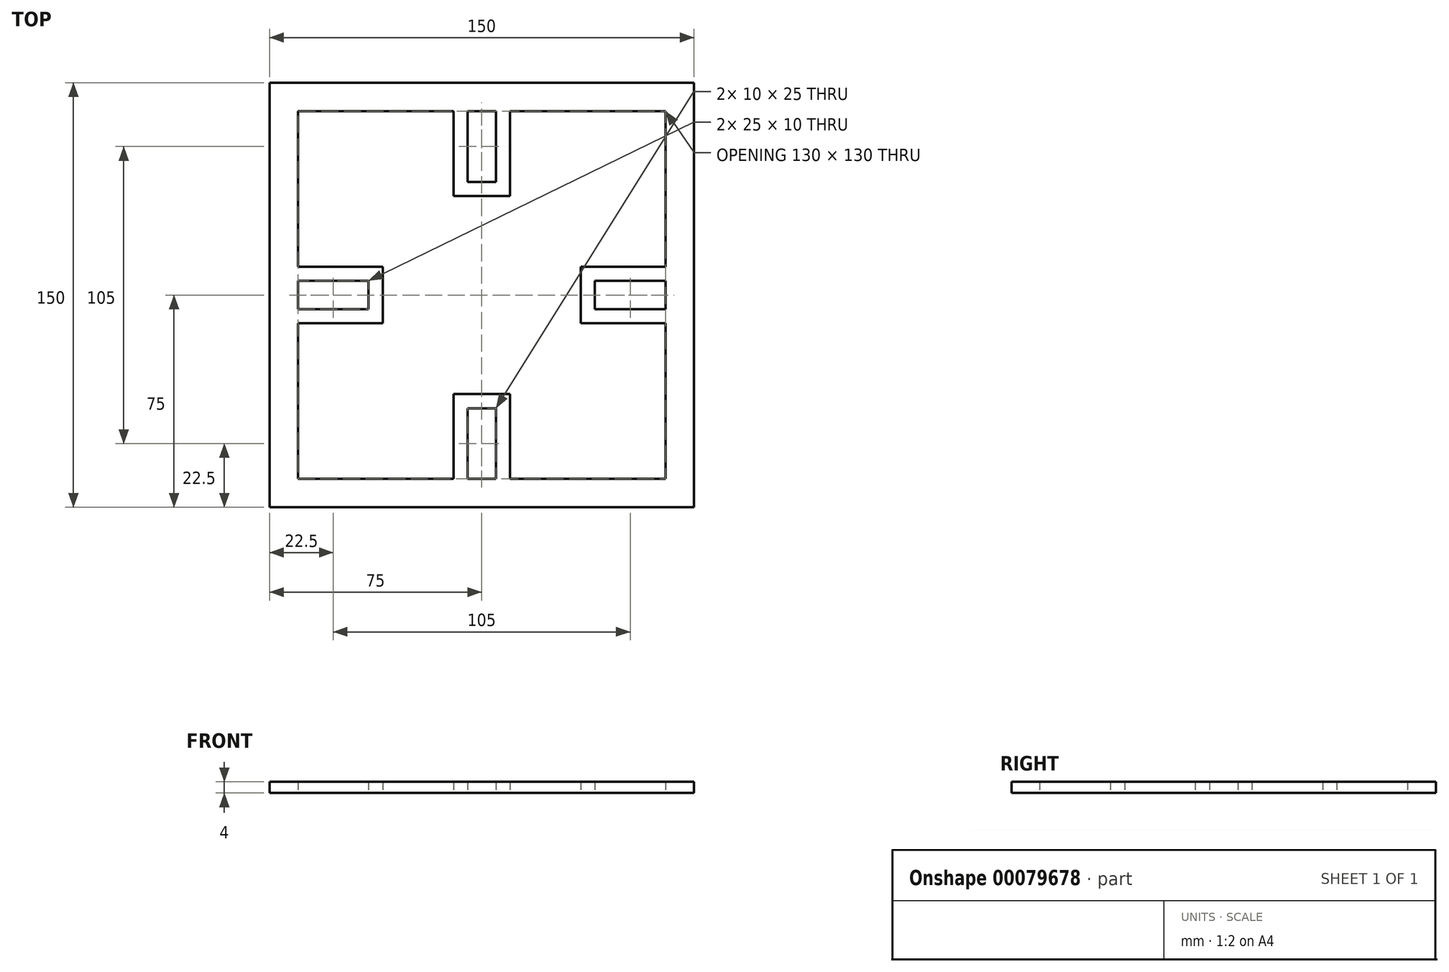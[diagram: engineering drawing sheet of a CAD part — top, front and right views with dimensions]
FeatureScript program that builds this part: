
annotation { "Feature Type Name" : "Feature", "Feature Type Description" : "" }
export const myFeature = defineFeature(function(context is Context, id is Id, definition is map)
    precondition{}
    {
        {
            var Q0;
            Q0=qCreatedBy(makeId("Top.planeOp"),FACE);
            var sketch = newSketch(context, id + "F0", { "sketchPlane" : qUnion([Q0])});
            skLineSegment(sketch, "E0.bottom", {"start": v(-75, 75) * mm, "end": v(75, 75) * mm});
            skLineSegment(sketch, "E0.top", {"start": v(-75, -75) * mm, "end": v(75, -75) * mm});
            skLineSegment(sketch, "E0.left", {"start": v(-75, 75) * mm, "end": v(-75, -75) * mm});
            skLineSegment(sketch, "E0.right", {"start": v(75, 75) * mm, "end": v(75, -75) * mm});
            skPoint(sketch, "E1", {"position": v(-75, 0) * mm});
            skPoint(sketch, "E2", {"position": v(0, 75) * mm});
            skLineSegment(sketch, "E3.bottom", {"start": v(-65, 65) * mm, "end": v(65, 65) * mm});
            skLineSegment(sketch, "E3.top", {"start": v(-65, -65) * mm, "end": v(65, -65) * mm});
            skLineSegment(sketch, "E3.left", {"start": v(-65, 65) * mm, "end": v(-65, -65) * mm});
            skLineSegment(sketch, "E3.right", {"start": v(65, 65) * mm, "end": v(65, -65) * mm});
            skSolve(sketch);
        }
        {
            var Q0;
            Q0=makeQuery(id+"F0.imprint","IMPRINT",FACE,{"disambiguationData":[TD([[makeQuery(id+"F0.imprint","IMPRINT",EDGE,{"derivedFrom":sQuery(id+"F0.wireOp",EDGE,"E0.bottom")}),-1.0]])]});
            extrude(context, id + "F1", {"entities" : qUnion([Q0]), "depth" : 4 * mm});
        }
        {
            var Q0;
            Q0=qCreatedBy(makeId("Top.planeOp"),FACE);
            var sketch = newSketch(context, id + "F2", { "sketchPlane" : qUnion([Q0])});
            skLineSegment(sketch, "E4.bottom", {"start": v(-10, 65) * mm, "end": v(10, 65) * mm});
            skLineSegment(sketch, "E4.top", {"start": v(-10, 35) * mm, "end": v(10, 35) * mm});
            skLineSegment(sketch, "E4.left", {"start": v(-10, 65) * mm, "end": v(-10, 35) * mm});
            skLineSegment(sketch, "E4.right", {"start": v(10, 65) * mm, "end": v(10, 35) * mm});
            skLineSegment(sketch, "E5.bottom", {"start": v(65, 10) * mm, "end": v(35, 10) * mm});
            skLineSegment(sketch, "E5.top", {"start": v(65, -10) * mm, "end": v(35, -10) * mm});
            skLineSegment(sketch, "E5.left", {"start": v(65, 10) * mm, "end": v(65, -10) * mm});
            skLineSegment(sketch, "E5.right", {"start": v(35, 10) * mm, "end": v(35, -10) * mm});
            skLineSegment(sketch, "E6.bottom", {"start": v(10, -65) * mm, "end": v(-10, -65) * mm});
            skLineSegment(sketch, "E6.top", {"start": v(10, -35) * mm, "end": v(-10, -35) * mm});
            skLineSegment(sketch, "E6.left", {"start": v(10, -65) * mm, "end": v(10, -35) * mm});
            skLineSegment(sketch, "E6.right", {"start": v(-10, -65) * mm, "end": v(-10, -35) * mm});
            skLineSegment(sketch, "E7.bottom", {"start": v(-65, 10) * mm, "end": v(-35, 10) * mm});
            skLineSegment(sketch, "E7.top", {"start": v(-65, -10) * mm, "end": v(-35, -10) * mm});
            skLineSegment(sketch, "E7.left", {"start": v(-65, 10) * mm, "end": v(-65, -10) * mm});
            skLineSegment(sketch, "E7.right", {"start": v(-35, 10) * mm, "end": v(-35, -10) * mm});
            skPoint(sketch, "E8", {"position": v(0, 35) * mm});
            skPoint(sketch, "E9", {"position": v(-35, 0) * mm});
            skPoint(sketch, "E10", {"position": v(35, 0) * mm});
            skPoint(sketch, "E11", {"position": v(0, -35) * mm});
            skLineSegment(sketch, "E12.bottom", {"start": v(-65, 5) * mm, "end": v(-40, 5) * mm});
            skLineSegment(sketch, "E12.top", {"start": v(-65, -5) * mm, "end": v(-40, -5) * mm});
            skLineSegment(sketch, "E12.left", {"start": v(-65, 5) * mm, "end": v(-65, -5) * mm});
            skLineSegment(sketch, "E12.right", {"start": v(-40, 5) * mm, "end": v(-40, -5) * mm});
            skLineSegment(sketch, "E13.bottom", {"start": v(65, 5) * mm, "end": v(40, 5) * mm});
            skLineSegment(sketch, "E13.top", {"start": v(65, -5) * mm, "end": v(40, -5) * mm});
            skLineSegment(sketch, "E13.left", {"start": v(65, 5) * mm, "end": v(65, -5) * mm});
            skLineSegment(sketch, "E13.right", {"start": v(40, 5) * mm, "end": v(40, -5) * mm});
            skLineSegment(sketch, "E14.bottom", {"start": v(-5, 65) * mm, "end": v(5, 65) * mm});
            skLineSegment(sketch, "E14.top", {"start": v(-5, 40) * mm, "end": v(5, 40) * mm});
            skLineSegment(sketch, "E14.left", {"start": v(-5, 65) * mm, "end": v(-5, 40) * mm});
            skLineSegment(sketch, "E14.right", {"start": v(5, 65) * mm, "end": v(5, 40) * mm});
            skLineSegment(sketch, "E15.bottom", {"start": v(-5, -65) * mm, "end": v(5, -65) * mm});
            skLineSegment(sketch, "E15.top", {"start": v(-5, -40) * mm, "end": v(5, -40) * mm});
            skLineSegment(sketch, "E15.left", {"start": v(-5, -65) * mm, "end": v(-5, -40) * mm});
            skLineSegment(sketch, "E15.right", {"start": v(5, -65) * mm, "end": v(5, -40) * mm});
            skPoint(sketch, "E16", {"position": v(-40, 0) * mm});
            skPoint(sketch, "E17", {"position": v(40, 0) * mm});
            skPoint(sketch, "E18", {"position": v(0, 40) * mm});
            skPoint(sketch, "E19", {"position": v(0, -40) * mm});
            skSolve(sketch);
        }
        {
            var Q0;
            {var subQ1=sQuery(id+"F2.wireOp",EDGE,"E7.bottom");Q0=makeQuery(id+"F2.imprint","IMPRINT",FACE,{"disambiguationData":[TD([[makeQuery(id+"F2.imprint","IMPRINT",EDGE,{"derivedFrom":subQ1}),-1.0]])]});}
            var Q1;
            Q1=makeQuery(id+"F2.imprint","IMPRINT",FACE,{"disambiguationData":[TD([[makeQuery(id+"F2.imprint","IMPRINT",EDGE,{"derivedFrom":sQuery(id+"F2.wireOp",EDGE,"E4.top")}),1.0]])]});
            var Q2;
            {var subQ4=sQuery(id+"F2.wireOp",EDGE,"E5.bottom");Q2=makeQuery(id+"F2.imprint","IMPRINT",FACE,{"disambiguationData":[TD([[makeQuery(id+"F2.imprint","IMPRINT",EDGE,{"derivedFrom":subQ4}),1.0]])]});}
            var Q3;
            Q3=makeQuery(id+"F2.imprint","IMPRINT",FACE,{"disambiguationData":[TD([[makeQuery(id+"F2.imprint","IMPRINT",EDGE,{"derivedFrom":sQuery(id+"F2.wireOp",EDGE,"E6.top")}),1.0]])]});
            var Q4;
            Q4=makeQuery(id+"F1.opExtrude","CAP_FACE",FACE,{"disambiguationData":[OSD([sQuery(id+"F0.wireOp",EDGE,"E0.bottom"),sQuery(id+"F0.wireOp",EDGE,"E0.top"),sQuery(id+"F0.wireOp",EDGE,"E0.left"),sQuery(id+"F0.wireOp",EDGE,"E0.right"),sQuery(id+"F0.wireOp",EDGE,"E3.bottom"),sQuery(id+"F0.wireOp",EDGE,"E3.top"),sQuery(id+"F0.wireOp",EDGE,"E3.left"),sQuery(id+"F0.wireOp",EDGE,"E3.right")])],"isStart":false});
            extrude(context, id + "F3", {"entities" : qUnion([Q0, Q1, Q2, Q3]), "operationType" : NewBodyOperationType.ADD, "endBound" : BoundingType.UP_TO_SURFACE, "endBoundEntityFace" : qUnion([Q4]), "depth" : 25 * mm});
        }
    });
